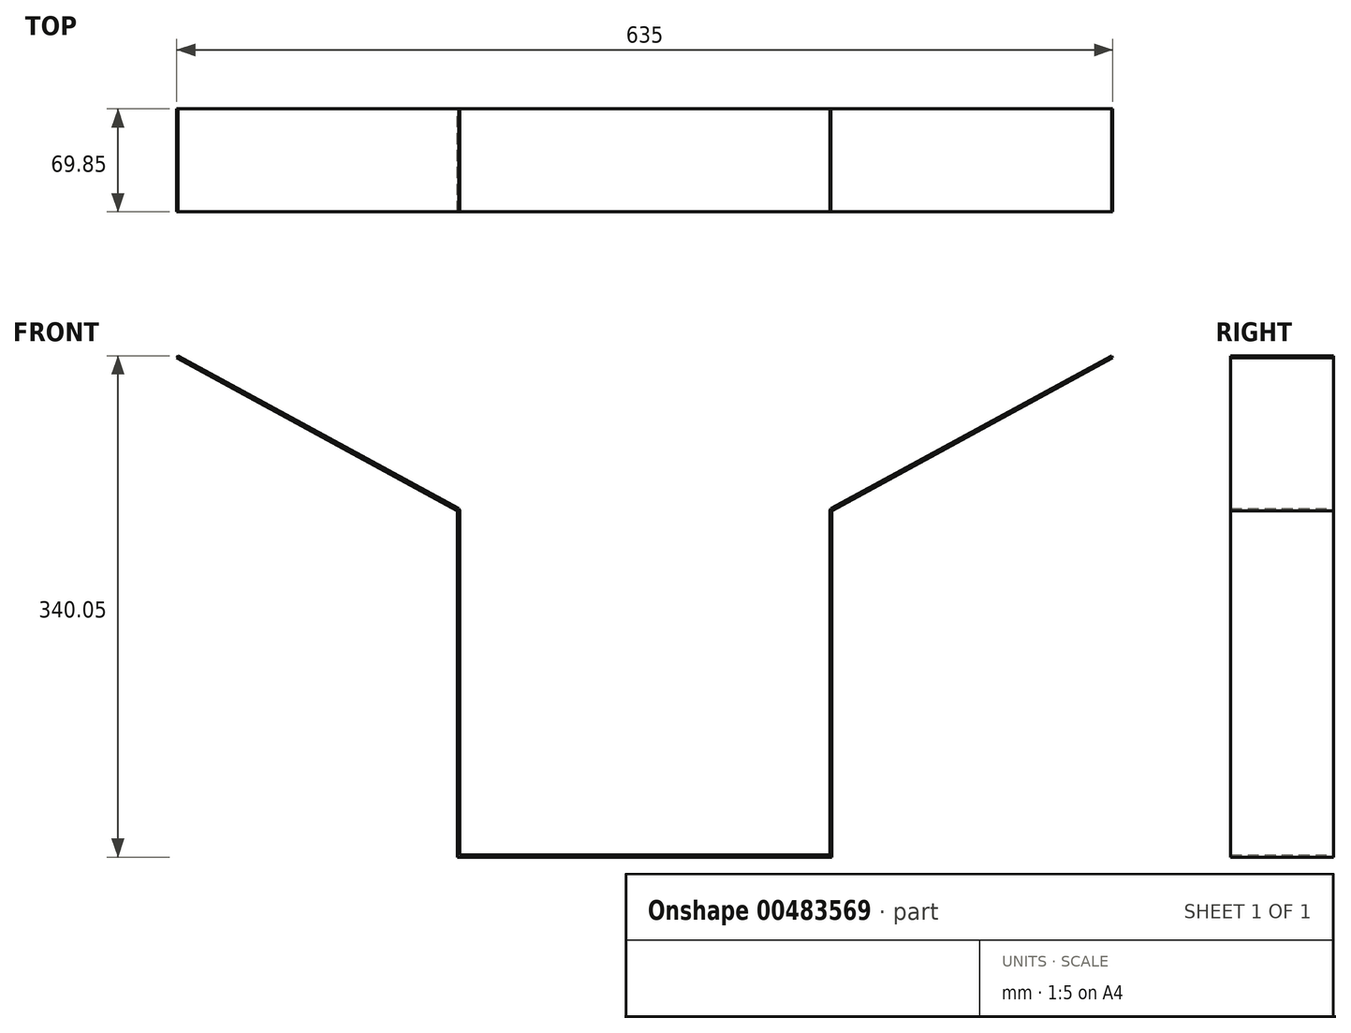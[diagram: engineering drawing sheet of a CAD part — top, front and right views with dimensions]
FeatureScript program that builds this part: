
annotation { "Feature Type Name" : "Feature", "Feature Type Description" : "" }
export const myFeature = defineFeature(function(context is Context, id is Id, definition is map)
    precondition{}
    {
        {
            var Q0;
            Q0=qCreatedBy(makeId("Front.planeOp"),FACE);
            var sketch = newSketch(context, id + "F0", { "sketchPlane" : qUnion([Q0])});
            skLineSegment(sketch, "E0.bottom", {"start": v(-138.35, -223.62) * mm, "end": v(115.65, -223.62) * mm});
            skLineSegment(sketch, "E1", {"start": v(115.65, -223.62) * mm, "end": v(115.65, 11.33) * mm});
            skPoint(sketch, "E1.endSnap0", {"position": v(306.15, 11.33) * mm});
            skLineSegment(sketch, "E2", {"start": v(115.65, 11.33) * mm, "end": v(306.15, 115.1) * mm});
            skLineSegment(sketch, "E3", {"start": v(-138.35, -223.62) * mm, "end": v(-138.35, 11.33) * mm});
            skLineSegment(sketch, "E4", {"start": v(-138.35, 11.33) * mm, "end": v(-328.85, 115.1) * mm});
            skLineSegment(sketch, "E5.0", {"start": v(114.13, -222.1) * mm, "end": v(114.13, 11.33) * mm});
            skLineSegment(sketch, "E6.0", {"start": v(114.92, 12.67) * mm, "end": v(305.42, 116.43) * mm});
            skLineSegment(sketch, "E7.0", {"start": v(-136.83, -222.1) * mm, "end": v(-136.83, 11.33) * mm});
            skLineSegment(sketch, "E8.0", {"start": v(-137.62, 12.67) * mm, "end": v(-328.12, 116.43) * mm});
            skPoint(sketch, "E9.orphan", {"position": v(306.15, -223.62) * mm});
            skPoint(sketch, "E0.top.end.orphan", {"position": v(306.15, 246.28) * mm});
            skLineSegment(sketch, "E10", {"start": v(-328.85, 115.1) * mm, "end": v(-328.12, 116.43) * mm});
            skLineSegment(sketch, "E11", {"start": v(305.42, 116.43) * mm, "end": v(306.15, 115.1) * mm});
            skLineSegment(sketch, "E12.0", {"start": v(-136.83, -222.1) * mm, "end": v(114.13, -222.1) * mm});
            skLineSegment(sketch, "E13", {"start": v(-137.62, 12.67) * mm, "end": v(-136.83, 11.33) * mm});
            skLineSegment(sketch, "E14", {"start": v(114.92, 12.67) * mm, "end": v(114.13, 11.33) * mm});
            skSolve(sketch);
        }
        {
            var Q0;
            Q0=makeQuery(id+"F0.imprint","IMPRINT",FACE,{"disambiguationData":[TD([[makeQuery(id+"F0.imprint","IMPRINT",EDGE,{"derivedFrom":sQuery(id+"F0.wireOp",EDGE,"E0.bottom")}),1.0]])]});
            extrude(context, id + "F1", {"entities" : qUnion([Q0]), "depth" : 69.85 * mm});
        }
    });
